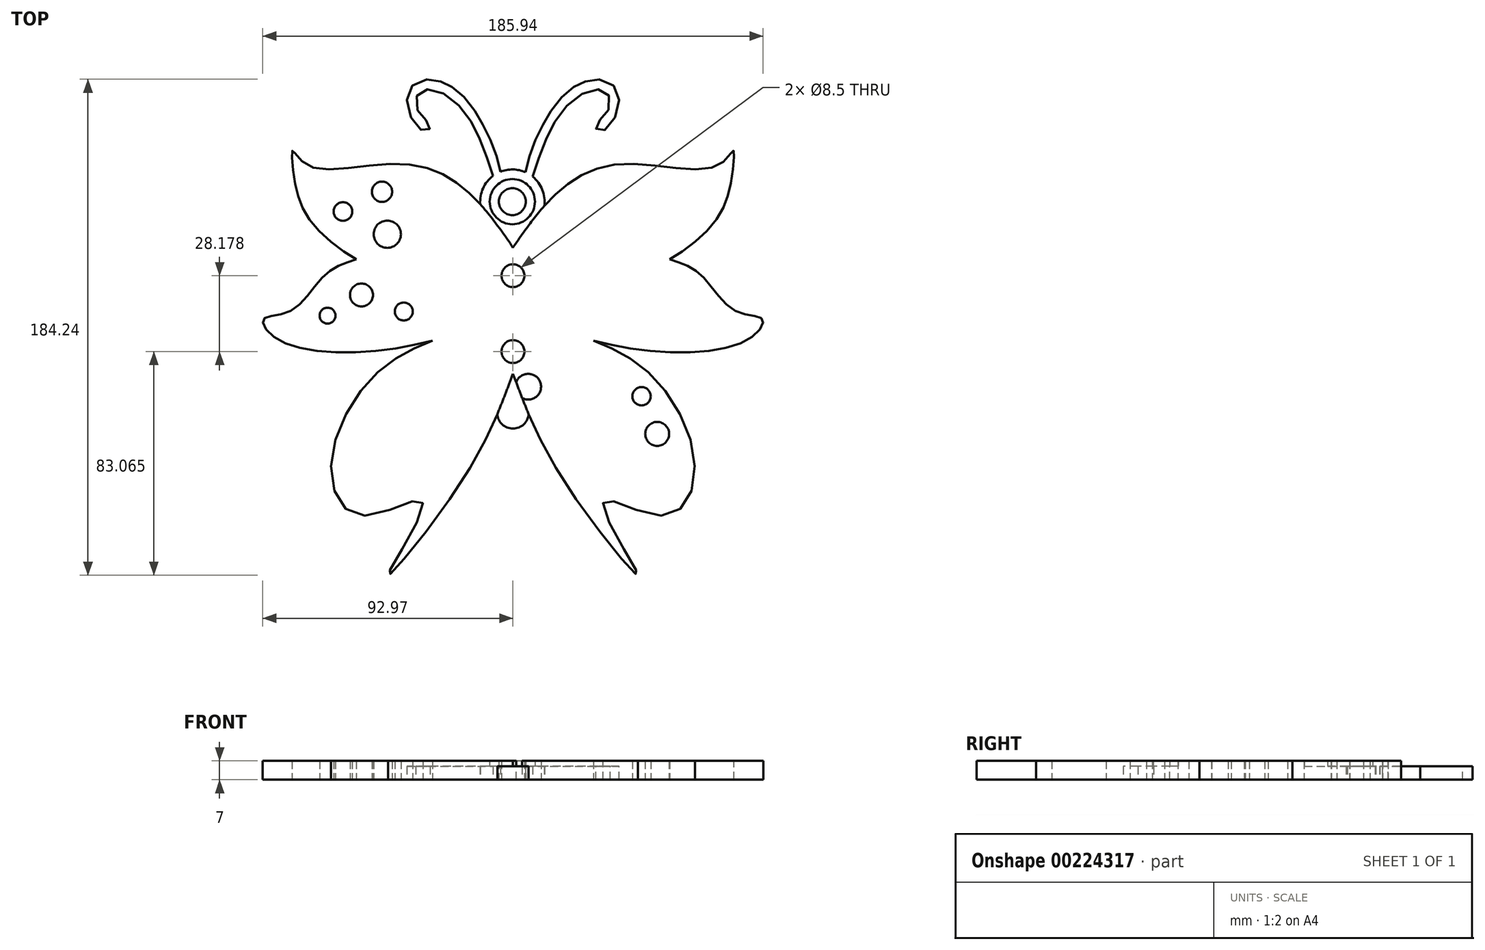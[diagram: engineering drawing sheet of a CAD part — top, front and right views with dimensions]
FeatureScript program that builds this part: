
annotation { "Feature Type Name" : "Feature", "Feature Type Description" : "" }
export const myFeature = defineFeature(function(context is Context, id is Id, definition is map)
    precondition{}
    {
        {
            var Q0;
            Q0=qCreatedBy(makeId("Top.planeOp"),FACE);
            var sketch = newSketch(context, id + "F0", { "sketchPlane" : qUnion([Q0])});
            skFitSpline(sketch, "E0", {"points": [v(0, 30.82) * mm, v(16.27, 51.04) * mm, v(41.42, 61.89) * mm, v(76.43, 61.4) * mm, v(81.86, 66.82) * mm, v(81.37, 57.45) * mm, v(75.94, 41.67) * mm, v(58.19, 26.38) * mm, v(40.58, 20.46) * mm, v(0, 17.01) * mm], "startDerivative": vector(122.09, 176.84) * mm, "endDerivative": vector(-297.91, -16.75) * mm});
            skFitSpline(sketch, "E1.MirrorCS", {"points": [v(0, 30.82) * mm, v(-16.27, 51.04) * mm, v(-41.42, 61.89) * mm, v(-76.43, 61.4) * mm, v(-81.86, 66.82) * mm, v(-81.37, 57.45) * mm, v(-75.94, 41.67) * mm, v(-58.19, 26.38) * mm, v(-40.58, 20.46) * mm, v(0, 17.01) * mm], "startDerivative": vector(-122.09, 176.84) * mm, "endDerivative": vector(297.91, -16.75) * mm});
            skFitSpline(sketch, "E2", {"points": [v(58.19, 26.38) * mm, v(70.02, 20.46) * mm, v(82.85, 7.15) * mm, v(92.7, 4.2) * mm, v(86.8, -3.7) * mm, v(40.58, -6.16) * mm, v(0, 8.27) * mm], "startDerivative": vector(94.36, -29.28) * mm, "endDerivative": vector(-157.48, 76.81) * mm});
            skFitSpline(sketch, "E3.MirrorCS", {"points": [v(-58.19, 26.38) * mm, v(-70.02, 20.46) * mm, v(-82.85, 7.15) * mm, v(-92.7, 4.2) * mm, v(-86.8, -3.7) * mm, v(-40.58, -6.16) * mm, v(0, 8.27) * mm], "startDerivative": vector(-94.36, -29.28) * mm, "endDerivative": vector(157.48, 76.81) * mm});
            skFitSpline(sketch, "E4", {"points": [v(29.93, -3.73) * mm, v(50.8, -16.03) * mm, v(67.56, -50.05) * mm, v(55.72, -68.8) * mm, v(33.53, -63.86) * mm, v(46.35, -90.5) * mm, v(20.25, -57.93) * mm, v(0, -16.04) * mm], "startDerivative": vector(168, -73.57) * mm, "endDerivative": vector(-81.03, 216.6) * mm});
            skFitSpline(sketch, "E5.MirrorCS", {"points": [v(-29.93, -3.73) * mm, v(-50.8, -16.03) * mm, v(-67.56, -50.05) * mm, v(-55.72, -68.8) * mm, v(-33.53, -63.86) * mm, v(-46.35, -90.5) * mm, v(-20.25, -57.93) * mm, v(0, -16.04) * mm], "startDerivative": vector(-168, -73.57) * mm, "endDerivative": vector(81.03, 216.6) * mm});
            skArc(sketch, "E6", {"start": v(11.63, 46.3) * mm, "mid": v(0.06, 59.8) * mm, "end": v(-12.15, 46.88) * mm});
            skCircle(sketch, "E7", {"center": v(-0.23, 47.85) * mm, "radius": 5 * mm});
            skCircle(sketch, "E8", {"center": v(46.7, 35.76) * mm, "radius": 5.07 * mm});
            skCircle(sketch, "E9", {"center": v(48.66, 51.52) * mm, "radius": 3.77 * mm});
            skCircle(sketch, "E10", {"center": v(63.17, 44.18) * mm, "radius": 3.47 * mm});
            skCircle(sketch, "E11.MirrorC", {"center": v(-46.7, 35.76) * mm, "radius": 5.07 * mm});
            skCircle(sketch, "E12.MirrorC", {"center": v(-48.66, 51.52) * mm, "radius": 3.77 * mm});
            skCircle(sketch, "E13.MirrorC", {"center": v(-63.17, 44.18) * mm, "radius": 3.47 * mm});
            skCircle(sketch, "E14", {"center": v(56.28, 13.17) * mm, "radius": 4.27 * mm});
            skCircle(sketch, "E15", {"center": v(40.58, 7.04) * mm, "radius": 3.34 * mm});
            skCircle(sketch, "E16", {"center": v(68.91, 5.51) * mm, "radius": 2.95 * mm});
            skCircle(sketch, "E17.MirrorC", {"center": v(-56.28, 13.17) * mm, "radius": 4.27 * mm});
            skCircle(sketch, "E18.MirrorC", {"center": v(-40.58, 7.04) * mm, "radius": 3.34 * mm});
            skCircle(sketch, "E19.MirrorC", {"center": v(-68.91, 5.51) * mm, "radius": 2.95 * mm});
            skEllipse(sketch, "E20", {"center": v(-49.16, -54.45) * mm, "majorRadius": 8.8 * mm, "minorRadius": 4.7 * mm, "majorAxis": v(-0.58, -0.81)});
            skCircle(sketch, "E21", {"center": v(-53.59, -38.43) * mm, "radius": 4.44 * mm});
            skCircle(sketch, "E22", {"center": v(-47.8, -24.45) * mm, "radius": 3.4 * mm});
            skCircle(sketch, "E23.MirrorC", {"center": v(47.8, -24.45) * mm, "radius": 3.4 * mm});
            skCircle(sketch, "E24.MirrorC", {"center": v(53.59, -38.43) * mm, "radius": 4.44 * mm});
            skEllipse(sketch, "E25.MirrorC", {"center": v(49.16, -54.45) * mm, "majorRadius": 8.8 * mm, "minorRadius": 4.7 * mm, "majorAxis": v(0.58, -0.81)});
            skFitSpline(sketch, "E26", {"points": [v(0, 26.68) * mm, v(10.16, 36.57) * mm, v(20.05, 39.98) * mm, v(23.8, 38.61) * mm, v(27.2, 38.96) * mm, v(25.5, 32.48) * mm, v(13.23, 25.32) * mm, v(0, 26.68) * mm]});
            skFitSpline(sketch, "E27", {"points": [v(0, 2.65) * mm, v(12.46, -3.66) * mm, v(28.66, -15.52) * mm, v(36.3, -30.45) * mm, v(30.57, -32.36) * mm, v(25.21, -28.92) * mm, v(31.72, -44.22) * mm, v(19.85, -27) * mm, v(12.46, -14.76) * mm, v(5.38, -4.71) * mm, v(0, 0) * mm], "startDerivative": vector(116.85, -56.03) * mm, "endDerivative": vector(-70.6, 53.24) * mm});
            skFitSpline(sketch, "E28.MirrorC", {"points": [v(0, 26.68) * mm, v(-10.16, 36.57) * mm, v(-20.05, 39.98) * mm, v(-23.8, 38.61) * mm, v(-27.2, 38.96) * mm, v(-25.5, 32.48) * mm, v(-13.23, 25.32) * mm, v(0, 26.68) * mm]});
            skFitSpline(sketch, "E29.MirrorCS", {"points": [v(0, 2.65) * mm, v(-12.46, -3.66) * mm, v(-28.66, -15.52) * mm, v(-36.3, -30.45) * mm, v(-30.57, -32.36) * mm, v(-25.21, -28.92) * mm, v(-31.72, -44.22) * mm, v(-19.85, -27) * mm, v(-12.46, -14.76) * mm, v(-5.38, -4.71) * mm, v(0, 0) * mm], "startDerivative": vector(-116.85, -56.03) * mm, "endDerivative": vector(70.6, 53.24) * mm});
            skCircle(sketch, "E30", {"center": v(-0.23, 47.85) * mm, "radius": 8.4 * mm});
            skFitSpline(sketch, "E31", {"points": [v(0, 14.77) * mm, v(5.8, 15.68) * mm, v(14.72, 14.36) * mm, v(21.03, 8.27) * mm, v(24.17, 5.44) * mm, v(28.79, 5.4) * mm, v(26.73, 2.35) * mm, v(21.95, 1.39) * mm, v(14.52, 3.58) * mm, v(7.14, 8.27) * mm, v(0, 11.1) * mm], "startDerivative": vector(54.46, 10.88) * mm, "endDerivative": vector(-66.88, 11.7) * mm});
            skFitSpline(sketch, "E32.MirrorCS", {"points": [v(0, 14.77) * mm, v(-5.8, 15.68) * mm, v(-14.72, 14.36) * mm, v(-21.03, 8.27) * mm, v(-24.17, 5.44) * mm, v(-28.79, 5.4) * mm, v(-26.73, 2.35) * mm, v(-21.95, 1.39) * mm, v(-14.52, 3.58) * mm, v(-7.14, 8.27) * mm, v(0, 11.1) * mm], "startDerivative": vector(-54.46, 10.88) * mm, "endDerivative": vector(66.88, 11.7) * mm});
            skArc(sketch, "E33", {"start": v(-5.83, -31.05) * mm, "mid": v(0, -36.47) * mm, "end": v(5.83, -31.05) * mm});
            skArc(sketch, "E34", {"start": v(-1.2, -19.23) * mm, "mid": v(-10.13, -19.2) * mm, "end": v(-3.43, -25.12) * mm});
            skArc(sketch, "E35.MirrorCS", {"start": v(1.2, -19.23) * mm, "mid": v(10.13, -19.2) * mm, "end": v(3.43, -25.12) * mm});
            skEllipse(sketch, "E36", {"center": v(31.01, 49.54) * mm, "majorRadius": 7.5 * mm, "minorRadius": 4.09 * mm, "majorAxis": v(0.81, 0.58)});
            skEllipse(sketch, "E37.MirrorC", {"center": v(-31.01, 49.54) * mm, "majorRadius": 7.5 * mm, "minorRadius": 4.09 * mm, "majorAxis": v(-0.81, 0.58)});
            skFitSpline(sketch, "E38", {"points": [v(4.64, 58.77) * mm, v(6.9, 67.15) * mm, v(10.63, 75.42) * mm, v(14.6, 82.23) * mm, v(20.99, 89.36) * mm, v(25.57, 91.95) * mm, v(31.15, 93.34) * mm, v(37.92, 90.35) * mm, v(39.05, 82.56) * mm, v(34.7, 74.86) * mm, v(31.35, 74.19) * mm, v(31.15, 77) * mm, v(34.03, 79.55) * mm, v(36.13, 85.77) * mm, v(33.14, 89.36) * mm, v(25.37, 87.77) * mm, v(16.6, 79.21) * mm, v(11.25, 68.5) * mm, v(7.33, 57.12) * mm], "startDerivative": vector(28.17, 137.38) * mm, "endDerivative": vector(-50.64, -159.63) * mm});
            skFitSpline(sketch, "E39.MirrorCS", {"points": [v(-4.64, 58.77) * mm, v(-6.9, 67.15) * mm, v(-10.63, 75.42) * mm, v(-14.6, 82.23) * mm, v(-20.99, 89.36) * mm, v(-25.57, 91.95) * mm, v(-31.15, 93.34) * mm, v(-37.92, 90.35) * mm, v(-39.05, 82.56) * mm, v(-34.7, 74.86) * mm, v(-31.35, 74.19) * mm, v(-31.15, 77) * mm, v(-34.03, 79.55) * mm, v(-36.13, 85.77) * mm, v(-33.14, 89.36) * mm, v(-25.37, 87.77) * mm, v(-16.6, 79.21) * mm, v(-11.25, 68.5) * mm, v(-7.33, 57.12) * mm], "startDerivative": vector(-28.17, 137.38) * mm, "endDerivative": vector(50.64, -159.63) * mm});
            skCircle(sketch, "E40", {"center": v(0, 20.34) * mm, "radius": 4.25 * mm});
            skCircle(sketch, "E41", {"center": v(0, -7.84) * mm, "radius": 4.25 * mm});
            skSolve(sketch);
        }
        {
            var Q0;
            Q0=makeQuery(id+"F0.imprint","IMPRINT",FACE,{"disambiguationData":[TD([[makeQuery(id+"F0.imprint","IMPRINT",EDGE,{"derivedFrom":sQuery(id+"F0.wireOp",EDGE,"E8")}),-1.0]])]});
            var Q1;
            {var subQ3=sQuery(id+"F0.wireOp",EDGE,"E6");Q1=makeQuery(id+"F0.imprint","IMPRINT",FACE,{"disambiguationData":[TD([[makeQuery(id+"F0.imprint","IMPRINT",EDGE,{"derivedFrom":subQ3}),1.0]])]});}
            var Q2;
            Q2=makeQuery(id+"F0.imprint","IMPRINT",FACE,{"disambiguationData":[TD([[makeQuery(id+"F0.imprint","IMPRINT",EDGE,{"derivedFrom":sQuery(id+"F0.wireOp",EDGE,"E14")}),-1.0]])]});
            var Q3;
            Q3=makeQuery(id+"F0.imprint","IMPRINT",FACE,{"disambiguationData":[TD([[makeQuery(id+"F0.imprint","IMPRINT",EDGE,{"derivedFrom":sQuery(id+"F0.wireOp",EDGE,"E20")}),-1.0]])]});
            var Q4;
            {var subQ0=sQuery(id+"F0.wireOp",EDGE,"E33");Q4=makeQuery(id+"F0.imprint","IMPRINT",FACE,{"disambiguationData":[TD([[makeQuery(id+"F0.imprint","IMPRINT",EDGE,{"derivedFrom":subQ0}),1.0]])]});}
            var Q5;
            {var subQ0=sQuery(id+"F0.wireOp",EDGE,"E39.MirrorCS");var subQ1=sQuery(id+"F0.wireOp",EDGE,"E6");var subQ2=makeQuery(id+"F0.imprint","INTERSECT",VERTEX,{"disambiguationData":[OD(0.0)],"derivedFrom":[subQ1,subQ0]});Q5=makeQuery(id+"F0.imprint","IMPRINT",FACE,{"disambiguationData":[TD([[makeQuery(id+"F0.imprint","IMPRINT",EDGE,{"disambiguationData":[TD([[subQ2,-1.0]])],"derivedFrom":subQ1}),-1.0]])]});}
            var Q6;
            {var subQ0=sQuery(id+"F0.wireOp",EDGE,"E38");Q6=makeQuery(id+"F0.imprint","IMPRINT",FACE,{"disambiguationData":[TD([[makeQuery(id+"F0.imprint","IMPRINT",EDGE,{"derivedFrom":subQ0}),-1.0]])]});}
            extrude(context, id + "F1", {"entities" : qUnion([Q0, Q1, Q2, Q3, Q4, Q5, Q6]), "depth" : 5 * mm});
        }
        {
            var Q0;
            Q0=makeQuery(id+"F0.imprint","IMPRINT",FACE,{"disambiguationData":[TD([[makeQuery(id+"F0.imprint","IMPRINT",EDGE,{"derivedFrom":sQuery(id+"F0.wireOp",EDGE,"E7")}),-1.0]])]});
            var Q1;
            {var subQ0=sQuery(id+"F0.wireOp",EDGE,"E28.MirrorC");var subQ1=sQuery(id+"F0.wireOp",EDGE,"E26");var subQ2=makeQuery(id+"F0.imprint","INTERSECT",VERTEX,{"disambiguationData":[OD(0.0)],"derivedFrom":[subQ1,subQ0]});Q1=makeQuery(id+"F0.imprint","IMPRINT",FACE,{"disambiguationData":[TD([[makeQuery(id+"F0.imprint","IMPRINT",EDGE,{"disambiguationData":[TD([[subQ2,1.0]])],"derivedFrom":subQ1}),-1.0]])]});}
            var Q2;
            {var subQ0=sQuery(id+"F0.wireOp",EDGE,"E28.MirrorC");var subQ1=sQuery(id+"F0.wireOp",EDGE,"E26");var subQ2=makeQuery(id+"F0.imprint","INTERSECT",VERTEX,{"disambiguationData":[OD(0.0)],"derivedFrom":[subQ1,subQ0]});Q2=makeQuery(id+"F0.imprint","IMPRINT",FACE,{"disambiguationData":[TD([[makeQuery(id+"F0.imprint","IMPRINT",EDGE,{"disambiguationData":[TD([[subQ2,-1.0]])],"derivedFrom":subQ1}),1.0]])]});}
            var Q3;
            {var subQ0=sQuery(id+"F0.wireOp",EDGE,"E28.MirrorC");var subQ1=sQuery(id+"F0.wireOp",EDGE,"E26");var subQ2=makeQuery(id+"F0.imprint","INTERSECT",VERTEX,{"disambiguationData":[OD(0.0)],"derivedFrom":[subQ1,subQ0]});Q3=makeQuery(id+"F0.imprint","IMPRINT",FACE,{"disambiguationData":[TD([[makeQuery(id+"F0.imprint","IMPRINT",EDGE,{"disambiguationData":[TD([[subQ2,-1.0]])],"derivedFrom":subQ1}),-1.0]])]});}
            var Q4;
            Q4=makeQuery(id+"F0.imprint","IMPRINT",FACE,{"disambiguationData":[TD([[makeQuery(id+"F0.imprint","IMPRINT",EDGE,{"derivedFrom":sQuery(id+"F0.wireOp",EDGE,"E31")}),-1.0]])]});
            var Q5;
            Q5=makeQuery(id+"F0.imprint","IMPRINT",FACE,{"disambiguationData":[TD([[makeQuery(id+"F0.imprint","IMPRINT",EDGE,{"derivedFrom":sQuery(id+"F0.wireOp",EDGE,"E8")}),1.0]])]});
            var Q6;
            Q6=makeQuery(id+"F0.imprint","IMPRINT",FACE,{"disambiguationData":[TD([[makeQuery(id+"F0.imprint","IMPRINT",EDGE,{"derivedFrom":sQuery(id+"F0.wireOp",EDGE,"E9")}),1.0]])]});
            var Q7;
            Q7=makeQuery(id+"F0.imprint","IMPRINT",FACE,{"disambiguationData":[TD([[makeQuery(id+"F0.imprint","IMPRINT",EDGE,{"derivedFrom":sQuery(id+"F0.wireOp",EDGE,"E10")}),1.0]])]});
            var Q8;
            Q8=makeQuery(id+"F0.imprint","IMPRINT",FACE,{"disambiguationData":[TD([[makeQuery(id+"F0.imprint","IMPRINT",EDGE,{"derivedFrom":sQuery(id+"F0.wireOp",EDGE,"E14")}),1.0]])]});
            var Q9;
            Q9=makeQuery(id+"F0.imprint","IMPRINT",FACE,{"disambiguationData":[TD([[makeQuery(id+"F0.imprint","IMPRINT",EDGE,{"derivedFrom":sQuery(id+"F0.wireOp",EDGE,"E15")}),1.0]])]});
            var Q10;
            Q10=makeQuery(id+"F0.imprint","IMPRINT",FACE,{"disambiguationData":[TD([[makeQuery(id+"F0.imprint","IMPRINT",EDGE,{"derivedFrom":sQuery(id+"F0.wireOp",EDGE,"E16")}),1.0]])]});
            var Q11;
            Q11=makeQuery(id+"F0.imprint","IMPRINT",FACE,{"disambiguationData":[TD([[makeQuery(id+"F0.imprint","IMPRINT",EDGE,{"derivedFrom":sQuery(id+"F0.wireOp",EDGE,"E27")}),-1.0]])]});
            var Q12;
            {var subQ0=sQuery(id+"F0.wireOp",EDGE,"E35.MirrorCS");Q12=makeQuery(id+"F0.imprint","IMPRINT",FACE,{"disambiguationData":[TD([[makeQuery(id+"F0.imprint","IMPRINT",EDGE,{"derivedFrom":subQ0}),-1.0]])]});}
            var Q13;
            Q13=makeQuery(id+"F0.imprint","IMPRINT",FACE,{"disambiguationData":[TD([[makeQuery(id+"F0.imprint","IMPRINT",EDGE,{"derivedFrom":sQuery(id+"F0.wireOp",EDGE,"E23.MirrorC")}),-1.0]])]});
            var Q14;
            Q14=makeQuery(id+"F0.imprint","IMPRINT",FACE,{"disambiguationData":[TD([[makeQuery(id+"F0.imprint","IMPRINT",EDGE,{"derivedFrom":sQuery(id+"F0.wireOp",EDGE,"E24.MirrorC")}),-1.0]])]});
            var Q15;
            Q15=makeQuery(id+"F0.imprint","IMPRINT",FACE,{"disambiguationData":[TD([[makeQuery(id+"F0.imprint","IMPRINT",EDGE,{"derivedFrom":sQuery(id+"F0.wireOp",EDGE,"E25.MirrorC")}),1.0]])]});
            var Q16;
            Q16=makeQuery(id+"F0.imprint","IMPRINT",FACE,{"disambiguationData":[TD([[makeQuery(id+"F0.imprint","IMPRINT",EDGE,{"derivedFrom":sQuery(id+"F0.wireOp",EDGE,"E20")}),1.0]])]});
            var Q17;
            Q17=makeQuery(id+"F0.imprint","IMPRINT",FACE,{"disambiguationData":[TD([[makeQuery(id+"F0.imprint","IMPRINT",EDGE,{"derivedFrom":sQuery(id+"F0.wireOp",EDGE,"E21")}),1.0]])]});
            var Q18;
            Q18=makeQuery(id+"F0.imprint","IMPRINT",FACE,{"disambiguationData":[TD([[makeQuery(id+"F0.imprint","IMPRINT",EDGE,{"derivedFrom":sQuery(id+"F0.wireOp",EDGE,"E22")}),1.0]])]});
            var Q19;
            Q19=makeQuery(id+"F0.imprint","IMPRINT",FACE,{"disambiguationData":[TD([[makeQuery(id+"F0.imprint","IMPRINT",EDGE,{"derivedFrom":sQuery(id+"F0.wireOp",EDGE,"E18.MirrorC")}),-1.0]])]});
            var Q20;
            Q20=makeQuery(id+"F0.imprint","IMPRINT",FACE,{"disambiguationData":[TD([[makeQuery(id+"F0.imprint","IMPRINT",EDGE,{"derivedFrom":sQuery(id+"F0.wireOp",EDGE,"E17.MirrorC")}),-1.0]])]});
            var Q21;
            Q21=makeQuery(id+"F0.imprint","IMPRINT",FACE,{"disambiguationData":[TD([[makeQuery(id+"F0.imprint","IMPRINT",EDGE,{"derivedFrom":sQuery(id+"F0.wireOp",EDGE,"E19.MirrorC")}),-1.0]])]});
            var Q22;
            Q22=makeQuery(id+"F0.imprint","IMPRINT",FACE,{"disambiguationData":[TD([[makeQuery(id+"F0.imprint","IMPRINT",EDGE,{"derivedFrom":sQuery(id+"F0.wireOp",EDGE,"E13.MirrorC")}),-1.0]])]});
            var Q23;
            Q23=makeQuery(id+"F0.imprint","IMPRINT",FACE,{"disambiguationData":[TD([[makeQuery(id+"F0.imprint","IMPRINT",EDGE,{"derivedFrom":sQuery(id+"F0.wireOp",EDGE,"E11.MirrorC")}),-1.0]])]});
            var Q24;
            Q24=makeQuery(id+"F0.imprint","IMPRINT",FACE,{"disambiguationData":[TD([[makeQuery(id+"F0.imprint","IMPRINT",EDGE,{"derivedFrom":sQuery(id+"F0.wireOp",EDGE,"E12.MirrorC")}),-1.0]])]});
            var Q25;
            {var subQ0=sQuery(id+"F0.wireOp",EDGE,"E34");Q25=makeQuery(id+"F0.imprint","IMPRINT",FACE,{"disambiguationData":[TD([[makeQuery(id+"F0.imprint","IMPRINT",EDGE,{"derivedFrom":subQ0}),1.0]])]});}
            var Q26;
            Q26=makeQuery(id+"F0.imprint","IMPRINT",FACE,{"disambiguationData":[TD([[makeQuery(id+"F0.imprint","IMPRINT",EDGE,{"derivedFrom":sQuery(id+"F0.wireOp",EDGE,"E36")}),1.0]])]});
            var Q27;
            Q27=makeQuery(id+"F0.imprint","IMPRINT",FACE,{"disambiguationData":[TD([[makeQuery(id+"F0.imprint","IMPRINT",EDGE,{"derivedFrom":sQuery(id+"F0.wireOp",EDGE,"E37.MirrorC")}),1.0]])]});
            extrude(context, id + "F2", {"entities" : qUnion([Q0, Q1, Q2, Q3, Q4, Q5, Q6, Q7, Q8, Q9, Q10, Q11, Q12, Q13, Q14, Q15, Q16, Q17, Q18, Q19, Q20, Q21, Q22, Q23, Q24, Q25, Q26, Q27]), "operationType" : NewBodyOperationType.ADD, "depth" : 7 * mm});
        }
    });
